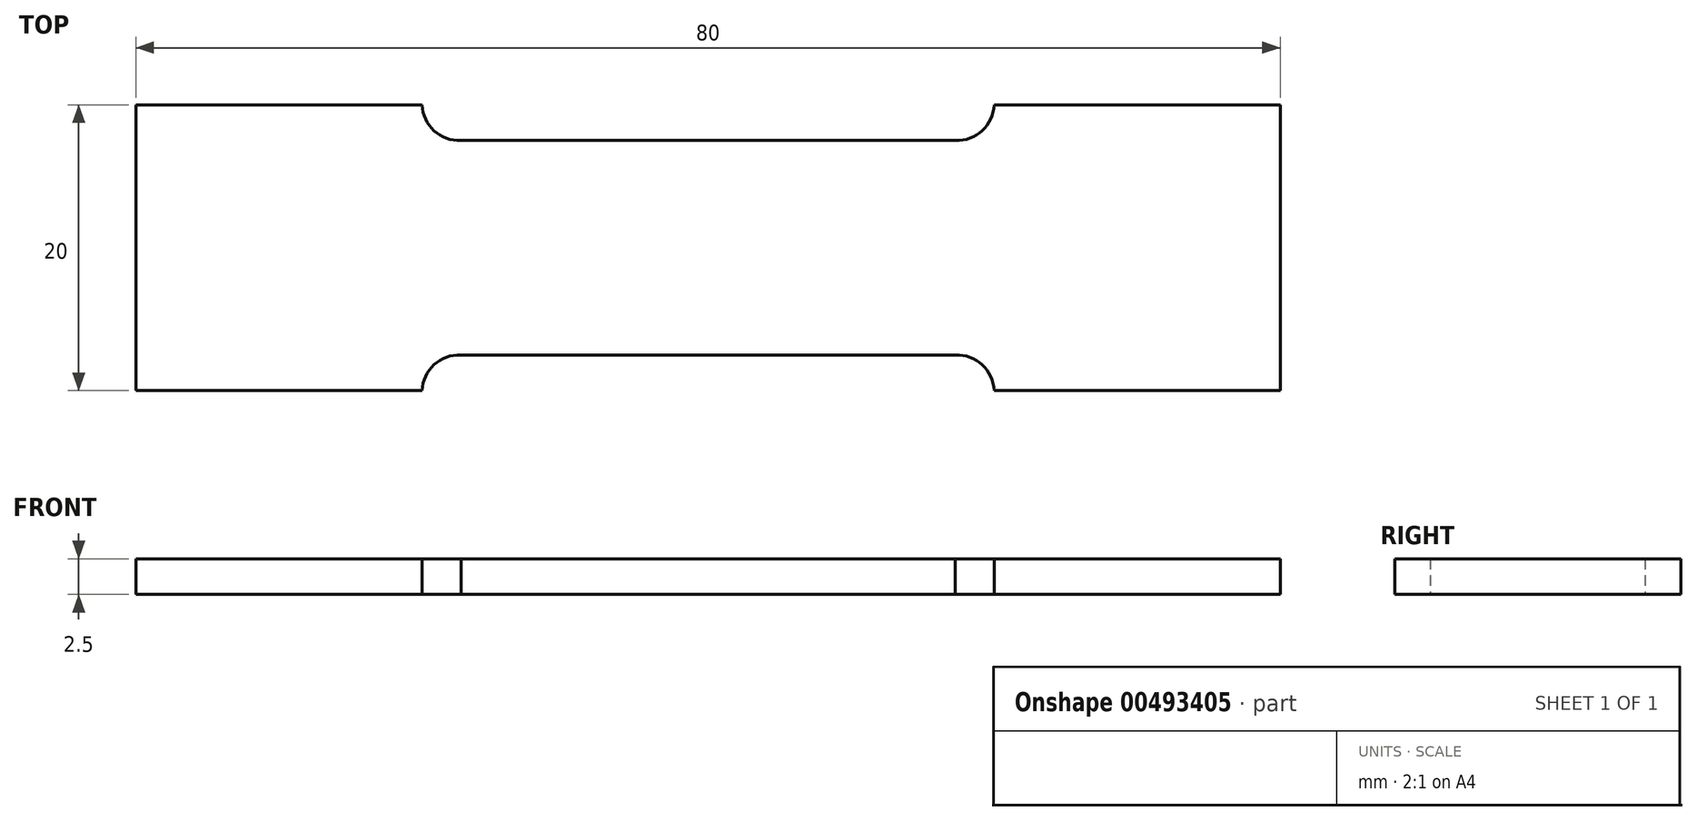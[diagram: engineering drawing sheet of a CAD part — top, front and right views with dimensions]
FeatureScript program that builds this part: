
annotation { "Feature Type Name" : "Feature", "Feature Type Description" : "" }
export const myFeature = defineFeature(function(context is Context, id is Id, definition is map)
    precondition{}
    {
        {
            var Q0;
            Q0=qCreatedBy(makeId("Top.planeOp"),FACE);
            var sketch = newSketch(context, id + "F0", { "sketchPlane" : qUnion([Q0])});
            skLineSegment(sketch, "E0.bottom", {"start": v(40, 10) * mm, "end": v(20, 10) * mm});
            skLineSegment(sketch, "E0.top", {"start": v(40, -10) * mm, "end": v(20, -10) * mm});
            skLineSegment(sketch, "E0.left", {"start": v(40, 10) * mm, "end": v(40, -10) * mm});
            skLineSegment(sketch, "E0.right", {"start": v(-40, 10) * mm, "end": v(-40, -10) * mm});
            skPoint(sketch, "E0.middle", {"position": v(0, 0) * mm});
            skLineSegment(sketch, "E1", {"start": v(-40, 10) * mm, "end": v(-20, 10) * mm});
            skLineSegment(sketch, "E2", {"start": v(-20, 10) * mm, "end": v(0, 10) * mm});
            skLineSegment(sketch, "E3", {"start": v(20, 10) * mm, "end": v(40, 10) * mm});
            skLineSegment(sketch, "E4", {"start": v(-20, -10) * mm, "end": v(-20, -7.5) * mm});
            skLineSegment(sketch, "E5", {"start": v(-20, 7.5) * mm, "end": v(17.5, 7.5) * mm});
            skLineSegment(sketch, "E6", {"start": v(-20, 7.5) * mm, "end": v(-17.5, 7.5) * mm});
            skArc(sketch, "E7", {"start": v(-20, 10) * mm, "mid": v(-19.16, 8.19) * mm, "end": v(-17.28, 7.5) * mm});
            skPoint(sketch, "E7.third.point", {"position": v(-19.14, 8.17) * mm});
            skLineSegment(sketch, "E8.MirrorCS", {"start": v(20, 10) * mm, "end": v(20, 7.5) * mm});
            skPoint(sketch, "E9.MirrorP", {"position": v(19.14, 8.17) * mm});
            skArc(sketch, "E10.MirrorCS", {"start": v(20, 10) * mm, "mid": v(19.16, 8.19) * mm, "end": v(17.28, 7.5) * mm});
            skPoint(sketch, "E11.MirrorP", {"position": v(-19.14, -8.17) * mm});
            skLineSegment(sketch, "E12.MirrorCS", {"start": v(-17.5, -7.5) * mm, "end": v(20, -7.5) * mm});
            skArc(sketch, "E13.MirrorCS", {"start": v(-20, -10) * mm, "mid": v(-19.16, -8.19) * mm, "end": v(-17.28, -7.5) * mm});
            skArc(sketch, "E14.MirrorCS", {"start": v(20, -10) * mm, "mid": v(19.16, -8.19) * mm, "end": v(17.28, -7.5) * mm});
            skPoint(sketch, "E15.MirrorP", {"position": v(19.14, -8.17) * mm});
            skLineSegment(sketch, "E16.MirrorCS", {"start": v(-20, -10) * mm, "end": v(0, -10) * mm});
            skLineSegment(sketch, "E17.trimOffspring", {"start": v(-20, -7.5) * mm, "end": v(-20, -10) * mm});
            skPoint(sketch, "E18.orphan", {"position": v(20, 7.5) * mm});
            skPoint(sketch, "E19.MirrorCS.end.orphan", {"position": v(17.5, -7.5) * mm});
            skPoint(sketch, "E20.MirrorCS.end.orphan", {"position": v(-17.5, -7.5) * mm});
            skPoint(sketch, "E21.MirrorCS.end.orphan", {"position": v(20, -7.5) * mm});
            skPoint(sketch, "E22.MirrorCS.end.orphan", {"position": v(20, -10) * mm});
            skLineSegment(sketch, "E23.trimOffspring", {"start": v(0, 10) * mm, "end": v(-40, 10) * mm});
            skLineSegment(sketch, "E24.trimOffspring", {"start": v(0, -10) * mm, "end": v(-40, -10) * mm});
            skSolve(sketch);
        }
        {
            var Q0;
            {var subQ9=sQuery(id+"F0.wireOp",EDGE,"E0.top");Q0=makeQuery(id+"F0.imprint","IMPRINT",FACE,{"disambiguationData":[TD([[makeQuery(id+"F0.imprint","IMPRINT",EDGE,{"derivedFrom":subQ9}),-1.0]])]});}
            extrude(context, id + "F1", {"entities" : qUnion([Q0]), "depth" : 2.5 * mm});
        }
    });
